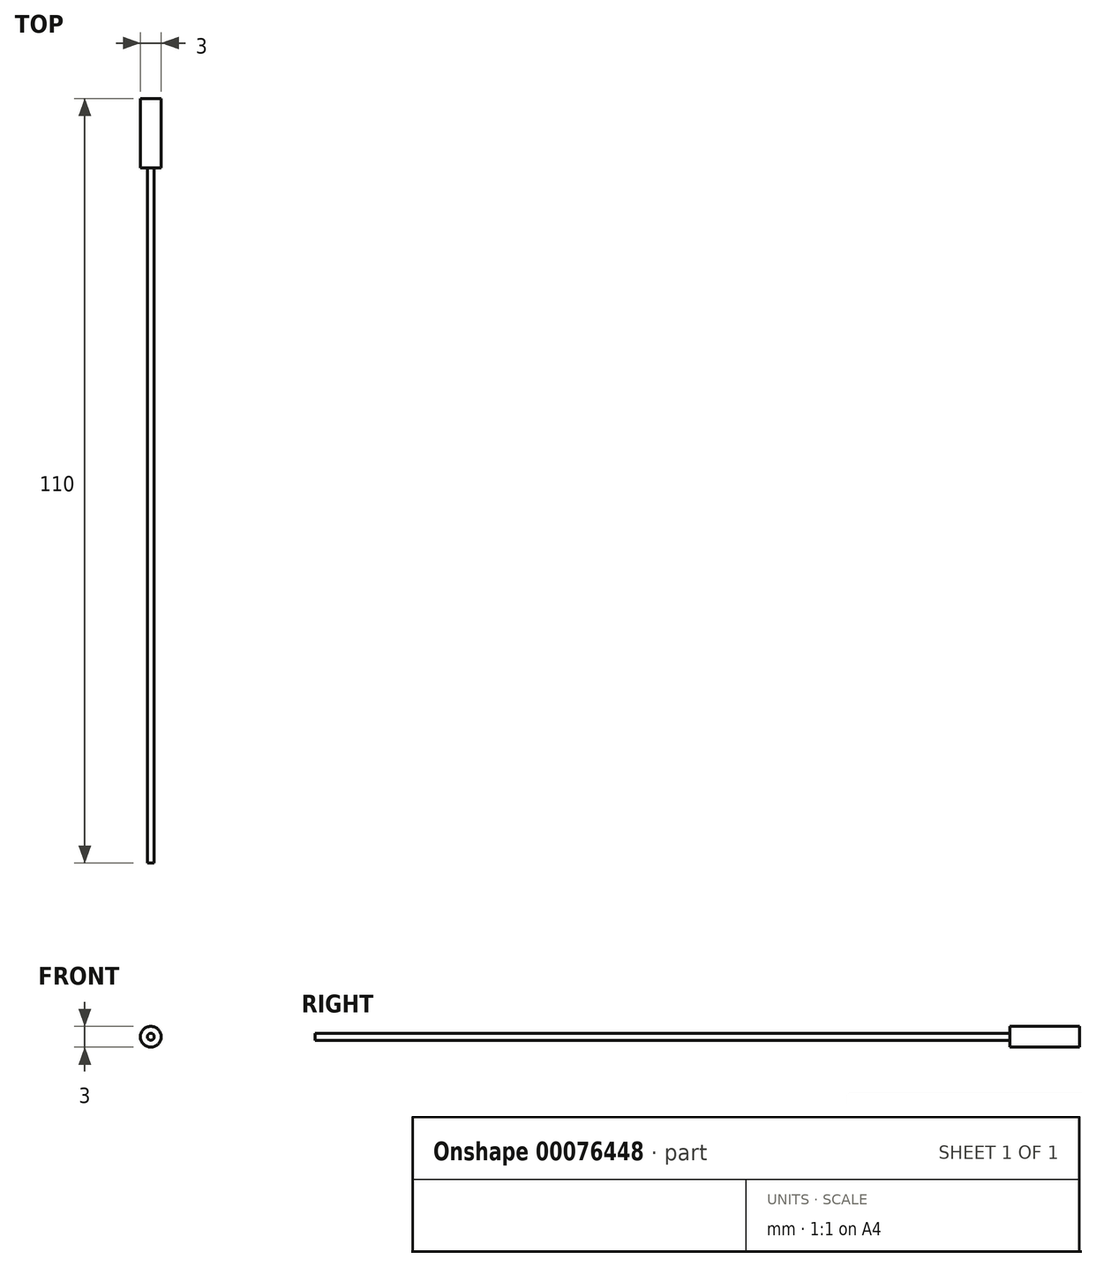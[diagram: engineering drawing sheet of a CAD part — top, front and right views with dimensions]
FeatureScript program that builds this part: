
annotation { "Feature Type Name" : "Feature", "Feature Type Description" : "" }
export const myFeature = defineFeature(function(context is Context, id is Id, definition is map)
    precondition{}
    {
        {
            var Q0;
            Q0=qCreatedBy(makeId("Front.planeOp"),FACE);
            var sketch = newSketch(context, id + "F0", { "sketchPlane" : qUnion([Q0])});
            skCircle(sketch, "E0", {"center": v(0, 0) * mm, "radius": 1.5 * mm});
            skCircle(sketch, "E1", {"center": v(0, 0) * mm, "radius": 0.5 * mm});
            skSolve(sketch);
        }
        {
            var Q0;
            Q0=makeQuery(id+"F0.imprint","IMPRINT",FACE,{"disambiguationData":[TD([[makeQuery(id+"F0.imprint","IMPRINT",EDGE,{"derivedFrom":sQuery(id+"F0.wireOp",EDGE,"E0")}),1.0]])]});
            var Q1;
            Q1=makeQuery(id+"F0.imprint","IMPRINT",FACE,{"disambiguationData":[TD([[makeQuery(id+"F0.imprint","IMPRINT",EDGE,{"derivedFrom":sQuery(id+"F0.wireOp",EDGE,"E1")}),1.0]])]});
            extrude(context, id + "F1", {"entities" : qUnion([Q0, Q1]), "oppositeDirection" : true, "depth" : 10 * mm});
        }
        {
            var Q0;
            Q0=makeQuery(id+"F0.imprint","IMPRINT",FACE,{"disambiguationData":[TD([[makeQuery(id+"F0.imprint","IMPRINT",EDGE,{"derivedFrom":sQuery(id+"F0.wireOp",EDGE,"E1")}),1.0]])]});
            extrude(context, id + "F2", {"entities" : qUnion([Q0]), "operationType" : NewBodyOperationType.ADD, "flatOperationType" : FlatOperationType.REMOVE, "offsetDistance" : 25 * mm, "depth" : 100 * mm, "domain" : OperationDomain.MODEL});
        }
    });
